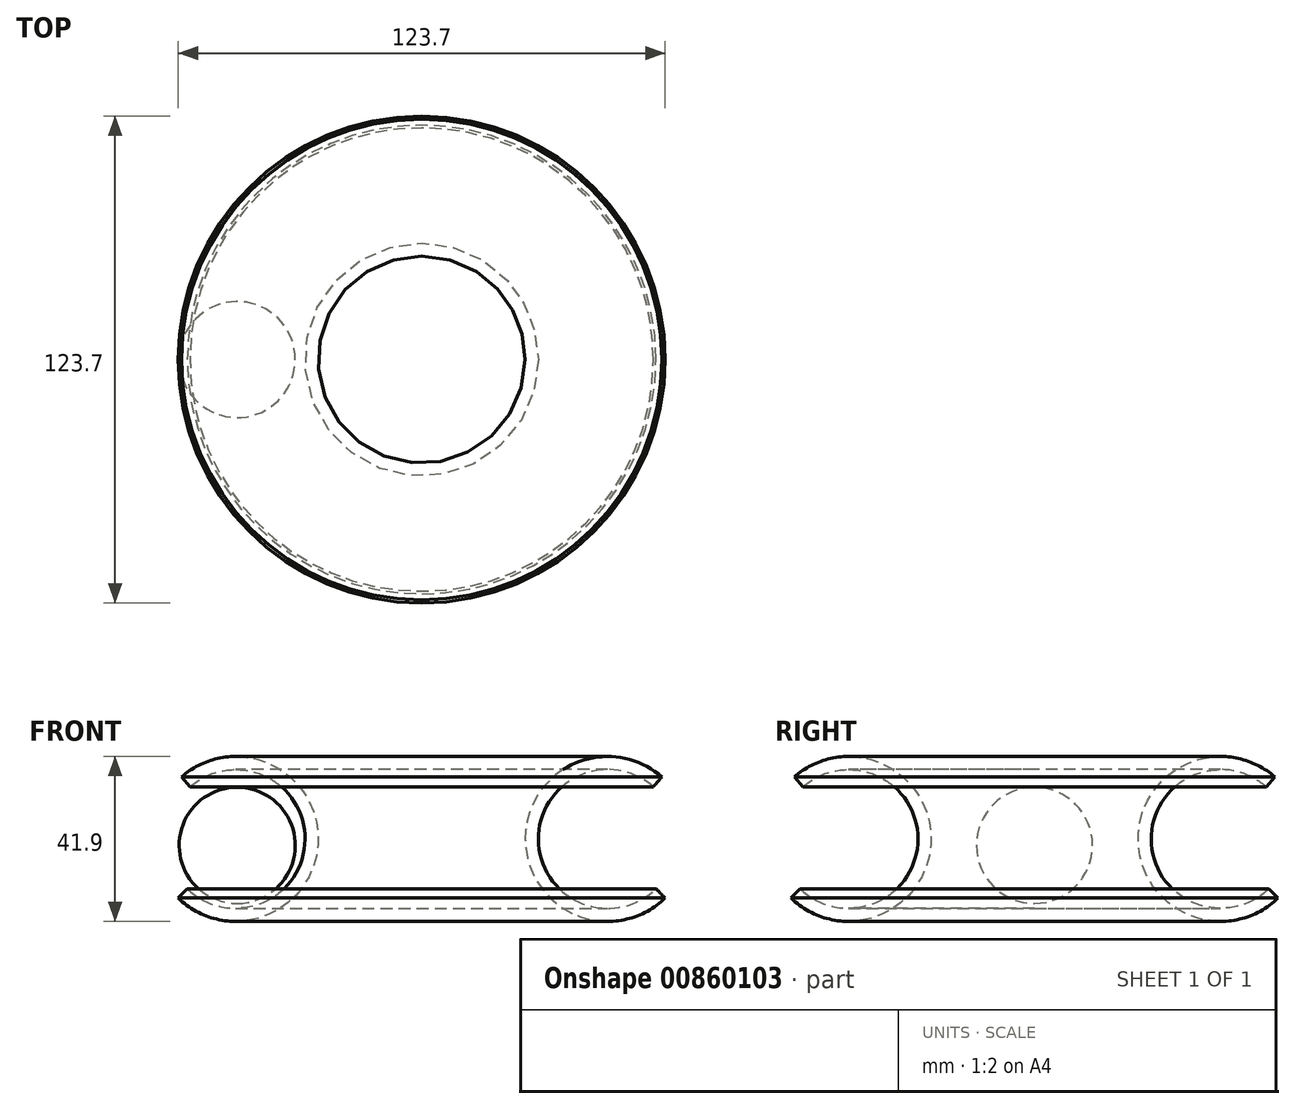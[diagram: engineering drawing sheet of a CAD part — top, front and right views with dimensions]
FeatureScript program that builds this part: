
annotation { "Feature Type Name" : "Feature", "Feature Type Description" : "" }
export const myFeature = defineFeature(function(context is Context, id is Id, definition is map)
    precondition{}
    {
        {
            var Q0;
            Q0=qCreatedBy(makeId("Front.planeOp"),FACE);
            var sketch = newSketch(context, id + "F0", { "sketchPlane" : qUnion([Q0])});
            skArc(sketch, "E0", {"start": v(-61.85, -15.01) * mm, "mid": v(-26.31, -0.55) * mm, "end": v(-61.04, 15.76) * mm});
            skArc(sketch, "E1", {"start": v(-59.54, -12.63) * mm, "mid": v(-29.63, -0.46) * mm, "end": v(-58.85, 13.26) * mm});
            skLineSegment(sketch, "E2", {"start": v(-58.85, 13.26) * mm, "end": v(-61.04, 15.76) * mm});
            skLineSegment(sketch, "E3", {"start": v(0, 44.88) * mm, "end": v(0, -42.04) * mm, "construction": true});
            skLineSegment(sketch, "E4", {"start": v(-59.54, -12.63) * mm, "end": v(-61.85, -15.01) * mm});
            skSolve(sketch);
        }
        {
            var Q0;
            Q0=makeQuery(id+"F0.imprint","IMPRINT",FACE,{"disambiguationData":[TD([[makeQuery(id+"F0.imprint","IMPRINT",EDGE,{"derivedFrom":sQuery(id+"F0.wireOp",EDGE,"E0")}),1.0]])]});
            var Q1;
            Q1=sQuery(id+"F0.wireOp",EDGE,"E3");
            revolve(context, id + "F1", {"surfaceOperationType" : NewSurfaceOperationType.NEW, "entities" : qUnion([Q0]), "axis" : qUnion([Q1]), "revolveType" : RevolveType.FULL});
        }
        {
            var Q0;
            Q0=qCreatedBy(makeId("Front.planeOp"),FACE);
            var sketch = newSketch(context, id + "F2", { "sketchPlane" : qUnion([Q0])});
            skArc(sketch, "E5", {"start": v(-46.87, -16.39) * mm, "mid": v(-32.12, -1.64) * mm, "end": v(-46.87, 13.1) * mm});
            skLineSegment(sketch, "E6", {"start": v(-46.87, 13.1) * mm, "end": v(-46.87, -16.39) * mm});
            skSolve(sketch);
        }
        {
            var Q0;
            Q0 = qSketchRegion(id + "F2", true);
            var Q1;
            Q1=sQuery(id+"F2.wireOp",EDGE,"E6");
            revolve(context, id + "F3", {"surfaceOperationType" : NewSurfaceOperationType.NEW, "entities" : qUnion([Q0]), "axis" : qUnion([Q1]), "revolveType" : RevolveType.FULL});
        }
    });
